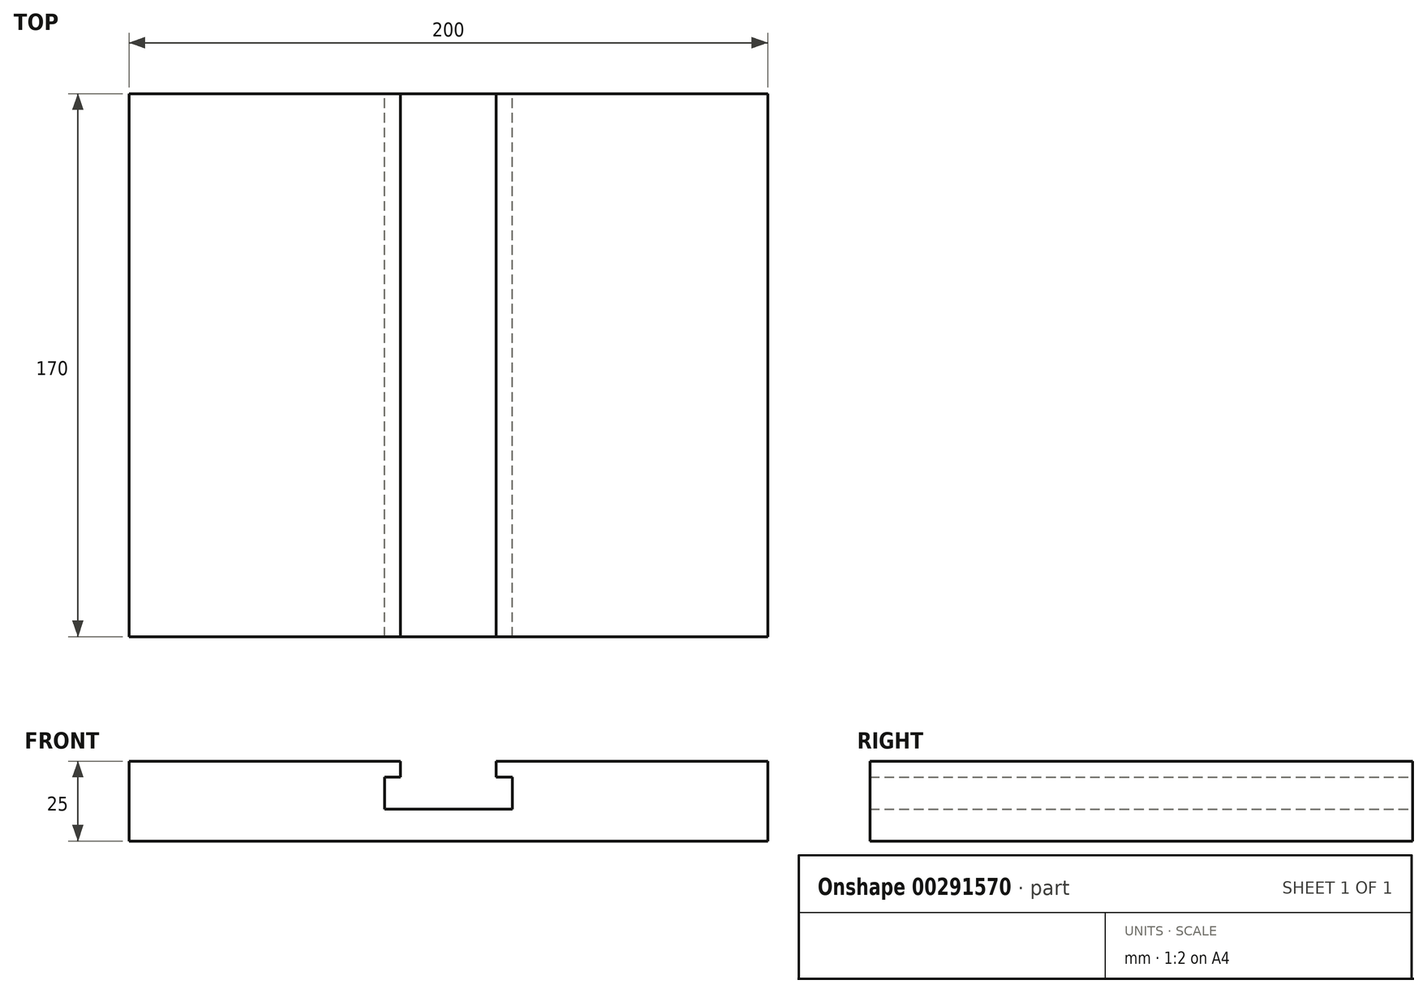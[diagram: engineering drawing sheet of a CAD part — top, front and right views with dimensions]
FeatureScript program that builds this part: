
annotation { "Feature Type Name" : "Feature", "Feature Type Description" : "" }
export const myFeature = defineFeature(function(context is Context, id is Id, definition is map)
    precondition{}
    {
        {
            var Q0;
            Q0=qCreatedBy(makeId("Right.planeOp"),FACE);
            var sketch = newSketch(context, id + "F0", { "sketchPlane" : qUnion([Q0])});
            skLineSegment(sketch, "E0.bottom", {"start": v(-85, 15) * mm, "end": v(85, 15) * mm});
            skLineSegment(sketch, "E0.top", {"start": v(-85, -10) * mm, "end": v(85, -10) * mm});
            skLineSegment(sketch, "E0.left", {"start": v(-85, 15) * mm, "end": v(-85, -10) * mm});
            skLineSegment(sketch, "E0.right", {"start": v(85, 15) * mm, "end": v(85, -10) * mm});
            skLineSegment(sketch, "E1", {"start": v(0, 26.75) * mm, "end": v(0, -27.25) * mm, "construction": true});
            skPoint(sketch, "E2.endSnap0", {"position": v(85, 2.5) * mm});
            skSolve(sketch);
        }
        {
            var Q0;
            Q0 = qSketchRegion(id + "F0", true);
            extrude(context, id + "F1", {"entities" : qUnion([Q0]), "oppositeDirection" : true, "depth" : 200 * mm});
        }
        {
            var Q0;
            Q0=makeQuery(id+"F1.opExtrude","SWEPT_FACE",FACE,{"disambiguationData":[OSD([sQuery(id+"F0.wireOp",EDGE,"E0.right")])]});
            var sketch = newSketch(context, id + "F2", { "sketchPlane" : qUnion([Q0])});
            skLineSegment(sketch, "E3", {"start": v(0, -10) * mm, "end": v(200, -10) * mm});
            skLineSegment(sketch, "E4", {"start": v(100, -10) * mm, "end": v(100, 15) * mm, "construction": true});
            skLineSegment(sketch, "E5.MirrorCS", {"start": v(200, -10) * mm, "end": v(0, -10) * mm, "construction": true});
            skLineSegment(sketch, "E6", {"start": v(115, 15) * mm, "end": v(115, 10) * mm});
            skLineSegment(sketch, "E7", {"start": v(115, 10) * mm, "end": v(120, 10) * mm});
            skLineSegment(sketch, "E8", {"start": v(120, 10) * mm, "end": v(120, 0) * mm});
            skLineSegment(sketch, "E9", {"start": v(120, 0) * mm, "end": v(100, 0) * mm});
            skLineSegment(sketch, "E10", {"start": v(115, 15) * mm, "end": v(100, 15) * mm});
            skLineSegment(sketch, "E11.MirrorCS", {"start": v(85, 10) * mm, "end": v(80, 10) * mm});
            skLineSegment(sketch, "E12.MirrorCS", {"start": v(80, 10) * mm, "end": v(80, 0) * mm});
            skLineSegment(sketch, "E13.MirrorCS", {"start": v(80, 0) * mm, "end": v(100, 0) * mm});
            skLineSegment(sketch, "E14.MirrorCS", {"start": v(85, 15) * mm, "end": v(100, 15) * mm});
            skLineSegment(sketch, "E15.MirrorCS", {"start": v(85, 15) * mm, "end": v(85, 10) * mm});
            skSolve(sketch);
        }
        {
            var Q0;
            Q0 = qSketchRegion(id + "F2", true);
            extrude(context, id + "F3", {"entities" : qUnion([Q0]), "operationType" : NewBodyOperationType.REMOVE, "endBound" : BoundingType.THROUGH_ALL, "oppositeDirection" : true, "depth" : 132 * mm});
        }
    });
